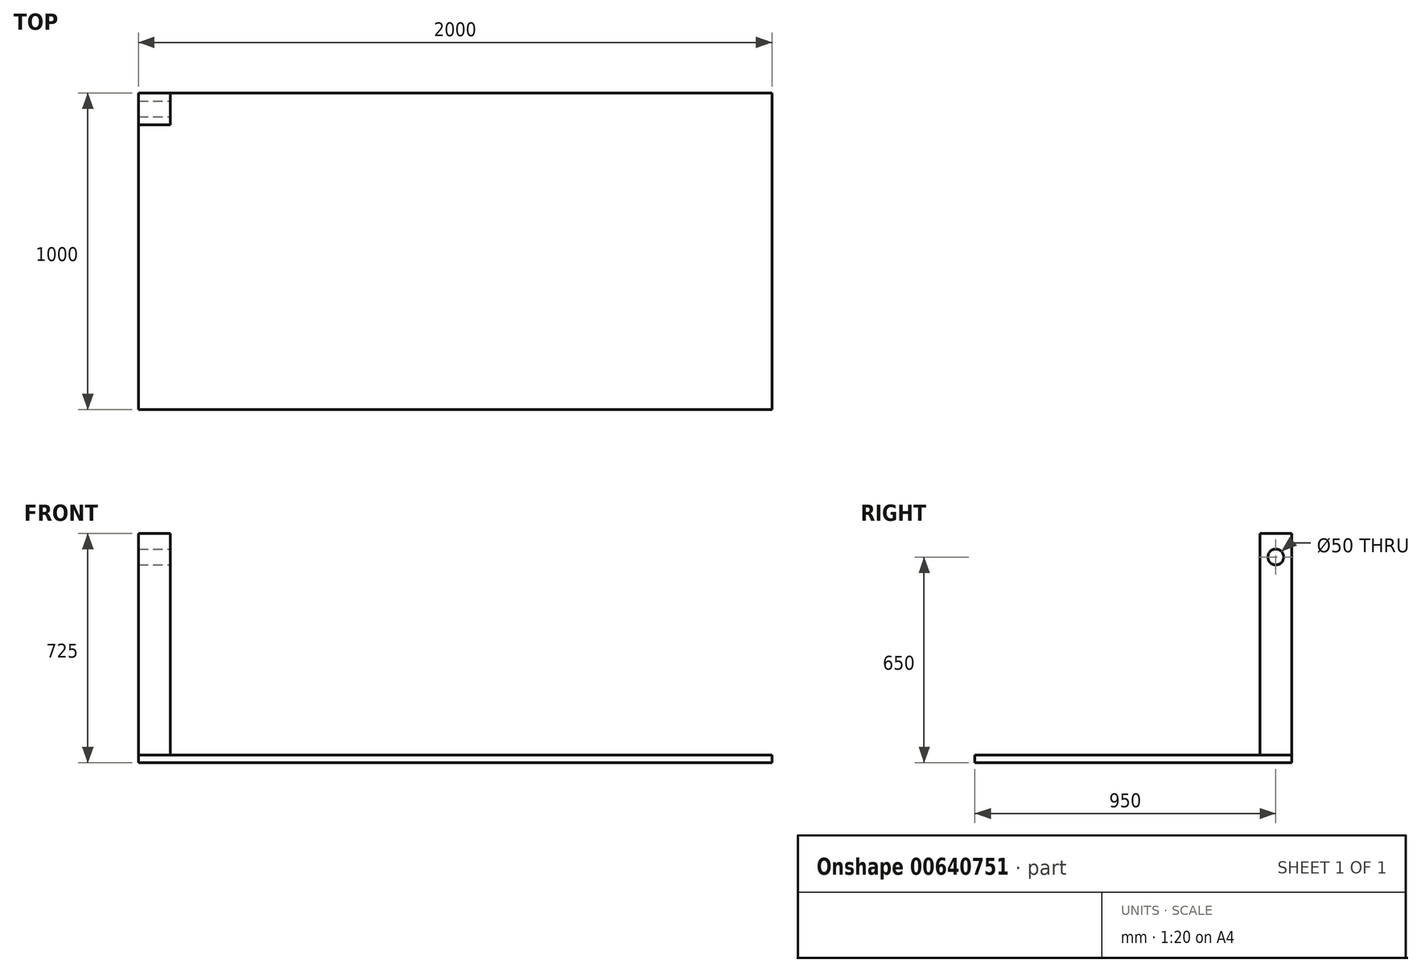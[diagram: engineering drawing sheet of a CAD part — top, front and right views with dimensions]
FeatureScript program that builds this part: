
annotation { "Feature Type Name" : "Feature", "Feature Type Description" : "" }
export const myFeature = defineFeature(function(context is Context, id is Id, definition is map)
    precondition{}
    {
        {
            assignVariable(context, id + "F0", {"name" : "hauteurp", "anyValue" : 700});
        }
        {
            assignVariable(context, id + "F1", {"name" : "epaisseurP", "anyValue" : 25});
        }
        {
            var Q0;
            Q0=qCreatedBy(makeId("Top.planeOp"),FACE);
            var sketch = newSketch(context, id + "F2", { "sketchPlane" : qUnion([Q0])});
            skLineSegment(sketch, "E0.bottom", {"start": v(-1000, 500) * mm, "end": v(1000, 500) * mm});
            skLineSegment(sketch, "E0.top", {"start": v(-1000, -500) * mm, "end": v(1000, -500) * mm});
            skLineSegment(sketch, "E0.left", {"start": v(-1000, 500) * mm, "end": v(-1000, -500) * mm});
            skLineSegment(sketch, "E0.right", {"start": v(1000, 500) * mm, "end": v(1000, -500) * mm});
            skSolve(sketch);
        }
        {
            var Q0;
            Q0 = qSketchRegion(id + "F2", true);
            extrude(context, id + "F3", {"entities" : qUnion([Q0]), "depth" : (getVariable(context, 'epaisseurP')) * mm, "offsetDistance" : 25 * mm});
        }
        {
            var Q0;
            Q0=makeQuery(id+"F3.opExtrude","CAP_FACE",FACE,{"disambiguationData":[OSD([sQuery(id+"F2.wireOp",EDGE,"E0.bottom"),sQuery(id+"F2.wireOp",EDGE,"E0.top"),sQuery(id+"F2.wireOp",EDGE,"E0.left"),sQuery(id+"F2.wireOp",EDGE,"E0.right")])],"isStart":false});
            var sketch = newSketch(context, id + "F4", { "sketchPlane" : qUnion([Q0])});
            skLineSegment(sketch, "E1.bottom", {"start": v(-1000, 500) * mm, "end": v(-900, 500) * mm});
            skLineSegment(sketch, "E1.top", {"start": v(-1000, 400) * mm, "end": v(-900, 400) * mm});
            skLineSegment(sketch, "E1.left", {"start": v(-1000, 500) * mm, "end": v(-1000, 400) * mm});
            skLineSegment(sketch, "E1.right", {"start": v(-900, 500) * mm, "end": v(-900, 400) * mm});
            skSolve(sketch);
        }
        {
            var Q0;
            Q0 = qSketchRegion(id + "F4", true);
            extrude(context, id + "F5", {"entities" : qUnion([Q0]), "operationType" : NewBodyOperationType.ADD, "depth" : (getVariable(context, 'hauteurp')) * mm, "offsetDistance" : 25 * mm});
        }
        {
            var Q0;
            Q0=makeQuery(id+"F5.opExtrude","SWEPT_FACE",FACE,{"disambiguationData":[OSD([sQuery(id+"F4.wireOp",EDGE,"E1.right")])]});
            var sketch = newSketch(context, id + "F6", { "sketchPlane" : qUnion([Q0])});
            skCircle(sketch, "E2", {"center": v(450, 650) * mm, "radius": 25 * mm});
            skSolve(sketch);
        }
        {
            var Q0;
            Q0 = qSketchRegion(id + "F6", true);
            extrude(context, id + "F7", {"entities" : qUnion([Q0]), "operationType" : NewBodyOperationType.REMOVE, "endBound" : BoundingType.UP_TO_NEXT, "oppositeDirection" : true, "depth" : 25 * mm, "offsetDistance" : 25 * mm});
        }
    });
